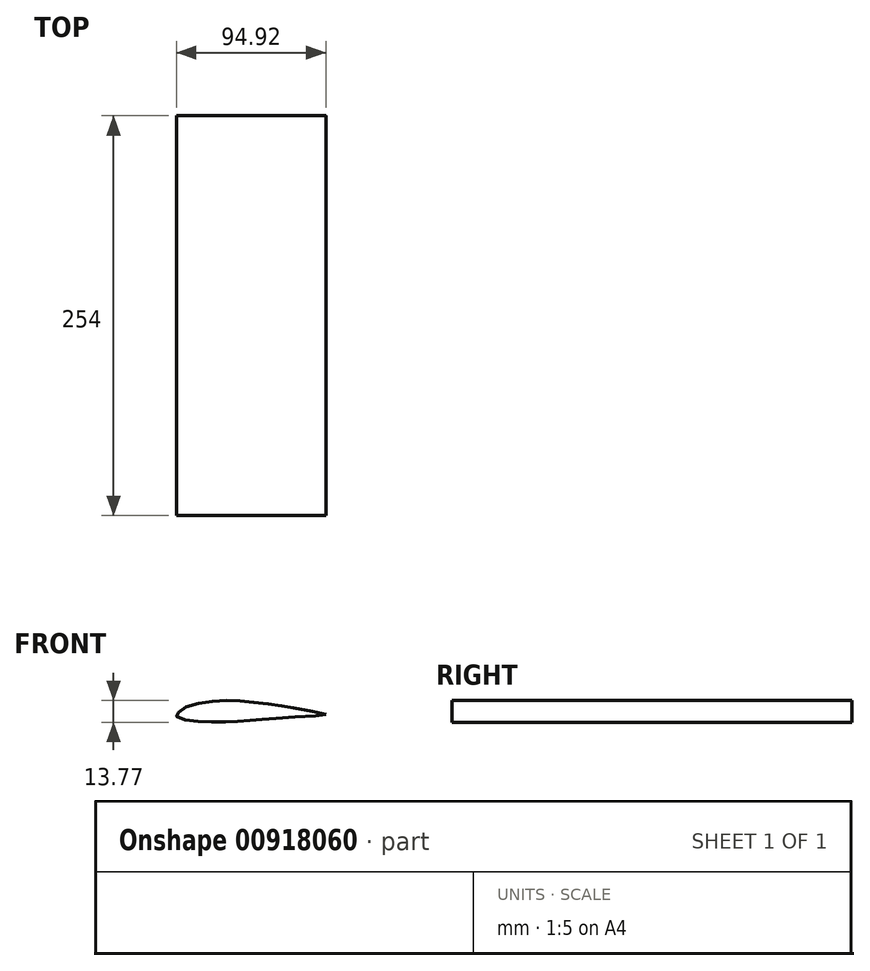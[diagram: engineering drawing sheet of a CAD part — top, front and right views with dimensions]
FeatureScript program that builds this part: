
annotation { "Feature Type Name" : "Feature", "Feature Type Description" : "" }
export const myFeature = defineFeature(function(context is Context, id is Id, definition is map)
    precondition{}
    {
        {
            var Q0;
            Q0=qCreatedBy(makeId("Front.planeOp"),FACE);
            var sketch = newSketch(context, id + "F0", { "sketchPlane" : qUnion([Q0])});
            skFitSpline(sketch, "E0", {"points": [v(94.68, 0) * mm, v(76.94, 3.78) * mm, v(66.27, 5.7) * mm, v(53.32, 7.38) * mm, v(40.73, 8.58) * mm, v(28.39, 8.82) * mm, v(15.44, 7.38) * mm, v(5, 4.5) * mm, v(1.05, 1.39) * mm, v(0, 0) * mm, v(0, -1.5) * mm, v(5.85, -3.4) * mm, v(17, -4.6) * mm, v(29.7, -4.85) * mm, v(39.53, -4.37) * mm, v(49.96, -3.4) * mm, v(59.91, -2.69) * mm, v(84.37, -1.01) * mm, v(94.68, 0) * mm]});
            skSolve(sketch);
        }
        {
            var Q0;
            Q0=makeQuery(id+"F0.imprint","IMPRINT",FACE,{"disambiguationData":[TD([[makeQuery(id+"F0.imprint","IMPRINT",EDGE,{"derivedFrom":sQuery(id+"F0.wireOp",EDGE,"E0")}),1.0]])]});
            extrude(context, id + "F1", {"entities" : qUnion([Q0]), "endBound" : BoundingType.SYMMETRIC, "depth" : 228.6 * mm, "offsetDistance" : 25.4 * mm});
        }
        {
            var Q0;
            Q0=makeQuery(id+"F1.opExtrude","CAP_FACE",FACE,{"disambiguationData":[OSD([sQuery(id+"F0.wireOp",EDGE,"E0")])],"isStart":false});
            extrude(context, id + "F2", {"entities" : qUnion([Q0]), "operationType" : NewBodyOperationType.ADD, "depth" : 25.4 * mm, "offsetDistance" : 25.4 * mm});
        }
    });
